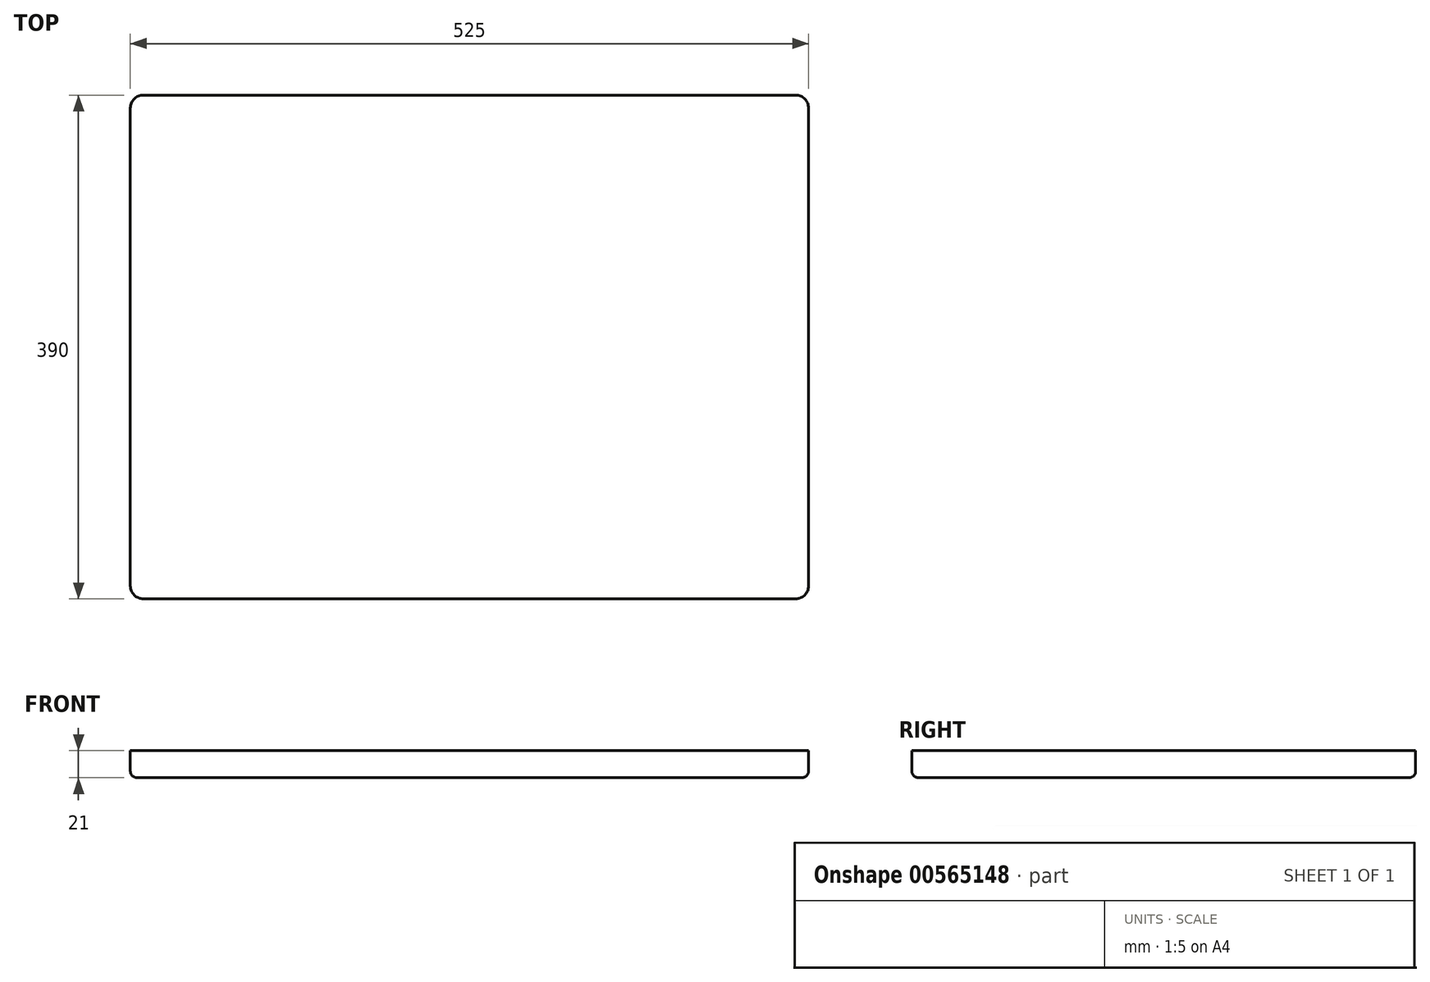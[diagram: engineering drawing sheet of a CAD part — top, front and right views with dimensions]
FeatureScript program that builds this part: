
annotation { "Feature Type Name" : "Feature", "Feature Type Description" : "" }
export const myFeature = defineFeature(function(context is Context, id is Id, definition is map)
    precondition{}
    {
        {
            var Q0;
            Q0=qCreatedBy(makeId("Top.planeOp"),FACE);
            var sketch = newSketch(context, id + "F0", { "sketchPlane" : qUnion([Q0])});
            skLineSegment(sketch, "E0.bottom", {"start": v(262.5, -195) * mm, "end": v(-262.5, -195) * mm});
            skLineSegment(sketch, "E0.top", {"start": v(262.5, 195) * mm, "end": v(-262.5, 195) * mm});
            skLineSegment(sketch, "E0.left", {"start": v(262.5, -195) * mm, "end": v(262.5, 195) * mm});
            skLineSegment(sketch, "E0.right", {"start": v(-262.5, -195) * mm, "end": v(-262.5, 195) * mm});
            skPoint(sketch, "E0.middle", {"position": v(0, 0) * mm});
            skSolve(sketch);
        }
        {
            var Q0;
            Q0 = qSketchRegion(id + "F0", true);
            var Q1;
            Q1=makeQuery(id+"F0.imprint","IMPRINT",FACE,{"disambiguationData":[TD([[makeQuery(id+"F0.imprint","IMPRINT",EDGE,{"derivedFrom":sQuery(id+"F0.wireOp",EDGE,"E0.bottom")}),-1.0]])]});
            extrude(context, id + "F1", {"entities" : qUnion([Q0, Q1]), "depth" : 21 * mm, "offsetDistance" : 25 * mm});
        }
        {
            var Q0;
            Q0=makeQuery(id+"F1.opExtrude","SWEPT_EDGE",EDGE,{"disambiguationData":[OSD([sQuery(id+"F0.wireOp",EDGE,"E0.top"),sQuery(id+"F0.wireOp",EDGE,"E0.right")])]});
            var Q1;
            Q1=makeQuery(id+"F1.opExtrude","SWEPT_EDGE",EDGE,{"disambiguationData":[OSD([sQuery(id+"F0.wireOp",EDGE,"E0.top"),sQuery(id+"F0.wireOp",EDGE,"E0.left")])]});
            var Q2;
            Q2=makeQuery(id+"F1.opExtrude","SWEPT_EDGE",EDGE,{"disambiguationData":[OSD([sQuery(id+"F0.wireOp",EDGE,"E0.bottom"),sQuery(id+"F0.wireOp",EDGE,"E0.left")])]});
            var Q3;
            Q3=makeQuery(id+"F1.opExtrude","SWEPT_EDGE",EDGE,{"disambiguationData":[OSD([sQuery(id+"F0.wireOp",EDGE,"E0.bottom"),sQuery(id+"F0.wireOp",EDGE,"E0.right")])]});
            fillet(context, id + "F2", {"entities" : qUnion([Q0, Q1, Q2, Q3]), "radius" : 10 * mm, "tangentPropagation" : true, "allowEdgeOverflow" : false});
        }
        {
            var Q0;
            Q0=makeQuery(id+"F1.opExtrude","CAP_EDGE",EDGE,{"disambiguationData":[OSD([sQuery(id+"F0.wireOp",EDGE,"E0.bottom")])],"isStart":true});
            fillet(context, id + "F3", {"entities" : qUnion([Q0]), "radius" : 5 * mm, "tangentPropagation" : true, "allowEdgeOverflow" : false});
        }
    });
